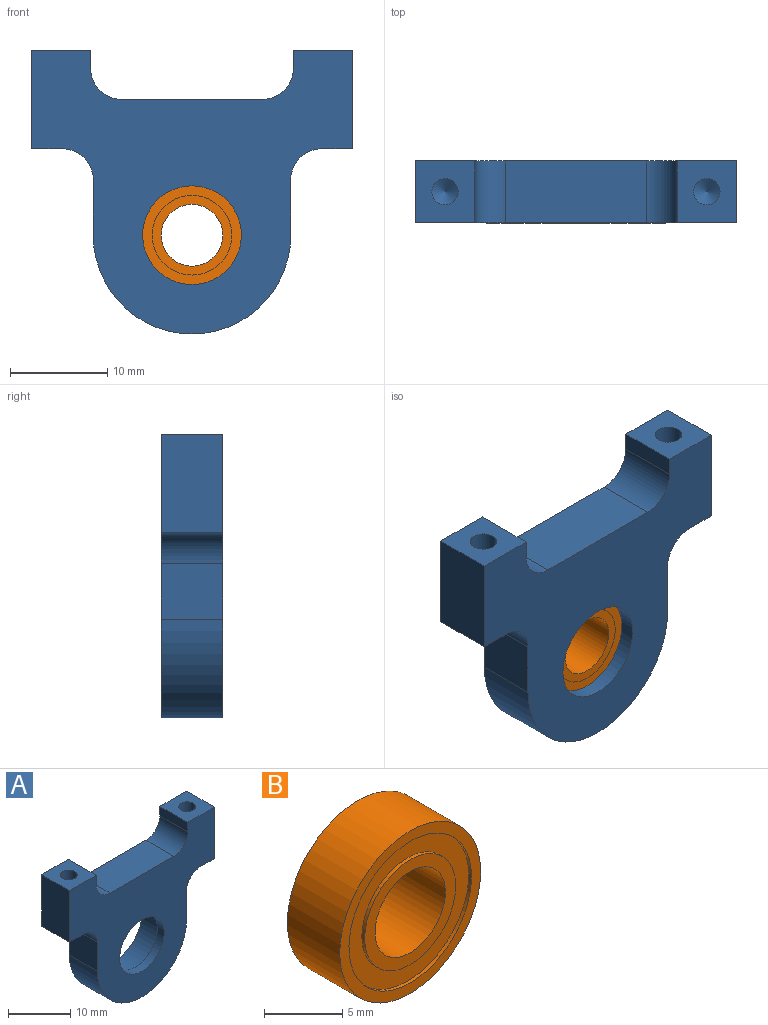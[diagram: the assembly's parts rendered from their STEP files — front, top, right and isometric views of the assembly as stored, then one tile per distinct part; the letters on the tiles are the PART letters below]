
ASSEMBLY  parts=2 mates=1
PART A: 25 faces, bbox 33x6.4x29.2 mm
  f0: cylinder r=5.08mm len=10.16mm, axis (0,1,0), area 50.3mm2, adj f19,f24
  f1: cylinder r=6.35mm len=12.7mm, axis (0,1,0), area 190.5mm2, adj f18,f24
  f2: cylinder r=1.35mm len=7.62mm, axis (0,0,1), area 64.8mm2, adj f3,f10
  f3: cone r=1.35mm half-angle=59deg, axis (0,0,1), area 6.7mm2, adj f2
  f4: cylinder r=1.35mm len=7.62mm, axis (0,0,1), area 64.8mm2, adj f5,f14
  f5: cone r=1.35mm half-angle=59deg, axis (0,0,1), area 6.7mm2, adj f4
  f6: cylinder r=10.16mm len=20.32mm, axis (0,-1,0), area 202.7mm2, adj f7,f17,f18,f19
  f7: plane 6.35x5.72mm, normal (-1,0,0), area 36.3mm2, adj f6,f18,f19,f20
  f8: plane 6.35x3.18mm, normal (0,0,-1), area 20.2mm2, adj f9,f18,f19,f20
  f9: plane 10.16x6.35mm, normal (-1,0,0), area 64.5mm2, adj f8,f10,f18,f19
  f10: plane 6.35x6.08mm, normal (0,0,1), area 32.9mm2, adj f2,f9,f11,f18,f19
  f11: plane 6.35x1.91mm, normal (1,0,0), area 12.1mm2, adj f10,f18,f19,f23
  f12: plane 14.51x6.35mm, normal (0,0,1), area 92.1mm2, adj f18,f19,f22,f23
  f13: plane 6.35x1.91mm, normal (-1,0,0), area 12.1mm2, adj f14,f18,f19,f22
  f14: plane 6.35x6.08mm, normal (0,0,1), area 32.9mm2, adj f4,f13,f15,f18,f19
  f15: plane 10.16x6.35mm, normal (1,0,0), area 64.5mm2, adj f14,f16,f18,f19
  f16: plane 6.35x3.18mm, normal (0,0,-1), area 20.2mm2, adj f15,f18,f19,f21
  f17: plane 6.35x5.72mm, normal (1,0,0), area 36.3mm2, adj f6,f18,f19,f21
  f18: plane 33.02x29.21mm, normal (0,1,0), area 454.3mm2, adj f1,f6,f7,f8,f9,f10,f11,f12
  f19: plane 33.02x29.21mm, normal (0,-1,0), area 499.9mm2, adj f0,f6,f7,f8,f9,f10,f11,f12
  f20: cylinder r=3.17mm len=6.35mm, axis (0,1,0), area 31.7mm2, adj f7,f8,f18,f19
  f21: cylinder r=3.17mm len=6.35mm, axis (0,1,0), area 31.7mm2, adj f16,f17,f18,f19
  f22: cylinder r=3.17mm len=6.35mm, axis (0,1,0), area 31.7mm2, adj f12,f13,f18,f19
  f23: cylinder r=3.17mm len=6.35mm, axis (0,1,0), area 31.7mm2, adj f11,f12,f18,f19
  f24: plane 12.7x12.7mm, normal (0,1,0), area 45.6mm2, adj f0,f1
PART B: 12 faces, bbox 12.7x4.7x12.7 mm
  f0: cylinder r=4.1mm len=8.2mm, axis (0,-1,0), area 6.5mm2, adj f6,f11
  f1: cylinder r=5.52mm len=11.05mm, axis (0,-1,0), area 8.8mm2, adj f9,f11
  f2: cylinder r=4.1mm len=8.2mm, axis (0,1,0), area 6.5mm2, adj f7,f10
  f3: cylinder r=5.52mm len=11.05mm, axis (0,1,0), area 8.8mm2, adj f8,f10
  f4: cylinder r=3.17mm len=6.35mm, axis (0,-1,0), area 94.2mm2, adj f6,f7
  f5: cylinder r=6.35mm len=12.7mm, axis (0,-1,0), area 188.5mm2, adj f8,f9
  f6: plane 8.2x8.2mm, normal (0,-1,0), area 21.2mm2, adj f0,f4
  f7: plane 8.2x8.2mm, normal (0,1,0), area 21.2mm2, adj f2,f4
  f8: plane 12.7x12.7mm, normal (0,1,0), area 30.8mm2, adj f3,f5
  f9: plane 12.7x12.7mm, normal (0,-1,0), area 30.8mm2, adj f1,f5
  f10: plane 11.05x11.05mm, normal (0,1,0), area 43mm2, adj f2,f3
  f11: plane 11.05x11.05mm, normal (0,-1,0), area 43mm2, adj f0,f1
PLACE A at identity
PLACE B t=(0,1.57,0)mm
MATE fastened B.f0 <-> A.f0  axis (0,-1,0) through (0,1.57,0)mm
